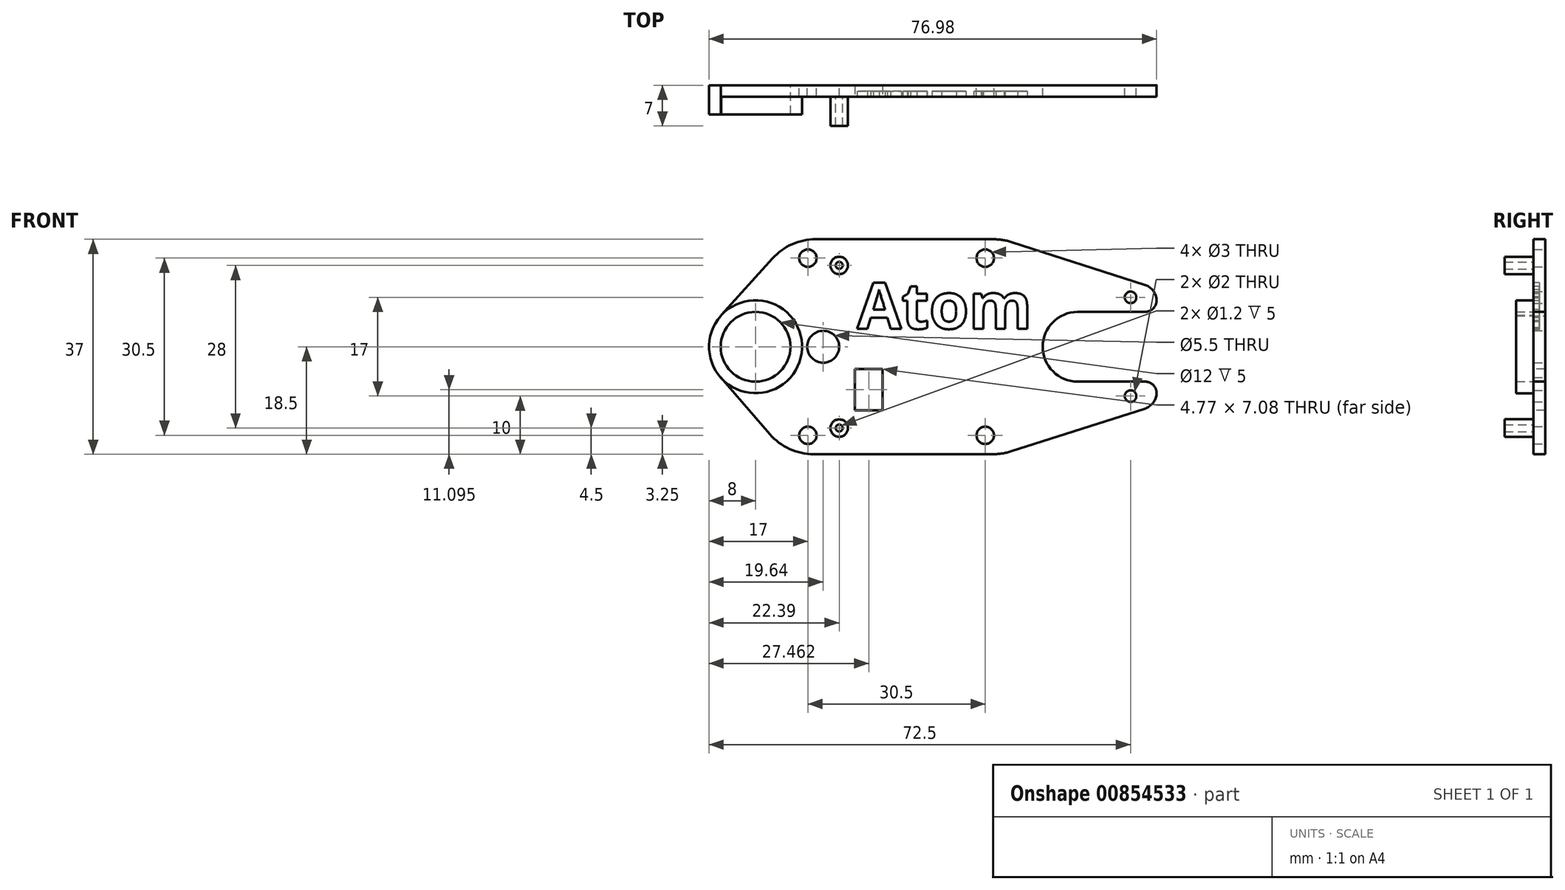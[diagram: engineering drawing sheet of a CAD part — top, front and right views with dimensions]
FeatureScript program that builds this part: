
annotation { "Feature Type Name" : "Feature", "Feature Type Description" : "" }
export const myFeature = defineFeature(function(context is Context, id is Id, definition is map)
    precondition{}
    {
        {
            var Q0;
            Q0=qCreatedBy(makeId("Front.planeOp"),FACE);
            var sketch = newSketch(context, id + "F0", { "sketchPlane" : qUnion([Q0])});
            skLineSegment(sketch, "E0.bottom", {"start": v(10.96, -18.5) * mm, "end": v(-26.06, -18.5) * mm});
            skLineSegment(sketch, "E0.top", {"start": v(11, 18.5) * mm, "end": v(-25.6, 18.5) * mm});
            skLineSegment(sketch, "E0.left", {"start": v(37.5, -10) * mm, "end": v(37.5, -6) * mm});
            skLineSegment(sketch, "E0.right", {"start": v(-37.5, -5.3) * mm, "end": v(-37.5, 5.3) * mm});
            skPoint(sketch, "E0.middle", {"position": v(0, 0) * mm});
            skPoint(sketch, "E1", {"position": v(-22.5, 15.25) * mm});
            skPoint(sketch, "E2", {"position": v(-22.5, -15.25) * mm});
            skPoint(sketch, "E3", {"position": v(8, 15.25) * mm});
            skPoint(sketch, "E4", {"position": v(8, -15.25) * mm});
            skPoint(sketch, "E5", {"position": v(33, 8.5) * mm});
            skPoint(sketch, "E6", {"position": v(33, -8.5) * mm});
            skCircle(sketch, "E7", {"center": v(-31.5, 0) * mm, "radius": 6 * mm});
            skCircle(sketch, "E8", {"center": v(-22.5, 15.25) * mm, "radius": 1.5 * mm});
            skCircle(sketch, "E9", {"center": v(-22.5, -15.25) * mm, "radius": 1.5 * mm});
            skCircle(sketch, "E10", {"center": v(8, 15.25) * mm, "radius": 1.5 * mm});
            skCircle(sketch, "E11", {"center": v(8, -15.25) * mm, "radius": 1.5 * mm});
            skCircle(sketch, "E12", {"center": v(33, 8.5) * mm, "radius": 1 * mm});
            skCircle(sketch, "E13", {"center": v(33, -8.5) * mm, "radius": 1 * mm});
            skCircle(sketch, "E14", {"center": v(-19.86, 0) * mm, "radius": 2.75 * mm});
            skCircle(sketch, "E15", {"center": v(-31.5, 0) * mm, "radius": 8 * mm});
            skLineSegment(sketch, "E16", {"start": v(-25.6, 18.5) * mm, "end": v(-37.5, 5.3) * mm});
            skLineSegment(sketch, "E17", {"start": v(-26.06, -18.5) * mm, "end": v(-37.5, -5.3) * mm});
            skPoint(sketch, "E18.orphan", {"position": v(-37.5, 18.5) * mm});
            skPoint(sketch, "E19.orphan", {"position": v(-37.5, -18.5) * mm});
            skPoint(sketch, "E20", {"position": v(37.5, -10) * mm});
            skPoint(sketch, "E21", {"position": v(37.5, 10) * mm});
            skLineSegment(sketch, "E22", {"start": v(11, 18.5) * mm, "end": v(37.5, 10) * mm});
            skLineSegment(sketch, "E23", {"start": v(10.96, -18.5) * mm, "end": v(37.5, -10) * mm});
            skPoint(sketch, "E24.orphan", {"position": v(37.5, 18.5) * mm});
            skPoint(sketch, "E25.orphan", {"position": v(37.5, -18.5) * mm});
            skPoint(sketch, "E26", {"position": v(37.5, 6) * mm});
            skPoint(sketch, "E27", {"position": v(37.5, -6) * mm});
            skLineSegment(sketch, "E28", {"start": v(37.5, 6) * mm, "end": v(23.9, 6) * mm});
            skLineSegment(sketch, "E29", {"start": v(37.5, -6) * mm, "end": v(23.9, -6) * mm});
            skArc(sketch, "E30", {"start": v(23.9, 6) * mm, "mid": v(17.9, 0) * mm, "end": v(23.9, -6) * mm});
            skLineSegment(sketch, "E31.trimOffspring", {"start": v(37.5, 6) * mm, "end": v(37.5, 10) * mm});
            skSolve(sketch);
        }
        {
            var Q0;
            Q0=makeQuery(id+"F0.imprint","IMPRINT",FACE,{"disambiguationData":[TD([[makeQuery(id+"F0.imprint","IMPRINT",EDGE,{"derivedFrom":sQuery(id+"F0.wireOp",EDGE,"E0.bottom")}),-1.0]])]});
            extrude(context, id + "F1", {"entities" : qUnion([Q0]), "depth" : 2 * mm, "offsetDistance" : 25 * mm});
        }
        {
            var Q0;
            {var subQ6=sQuery(id+"F0.wireOp",EDGE,"E7");Q0=makeQuery(id+"F0.imprint","IMPRINT",FACE,{"disambiguationData":[TD([[makeQuery(id+"F0.imprint","IMPRINT",EDGE,{"derivedFrom":subQ6}),-1.0]])]});}
            var Q1;
            {var subQ0=sQuery(id+"F0.wireOp",EDGE,"E15");var subQ1=sQuery(id+"F0.wireOp",EDGE,"E0.right");var subQ2=makeQuery(id+"F0.imprint","INTERSECT",VERTEX,{"derivedFrom":[subQ1,subQ0]});Q1=makeQuery(id+"F0.imprint","IMPRINT",FACE,{"disambiguationData":[TD([[makeQuery(id+"F0.imprint","IMPRINT",EDGE,{"disambiguationData":[TD([[subQ2,-1.0]])],"derivedFrom":subQ1}),1.0]])]});}
            extrude(context, id + "F2", {"entities" : qUnion([Q0, Q1]), "operationType" : NewBodyOperationType.ADD, "depth" : 5 * mm, "offsetDistance" : 25 * mm});
        }
        {
            var Q0;
            Q0=makeQuery(id+"F1.opExtrude","SWEPT_EDGE",EDGE,{"disambiguationData":[OSD([sQuery(id+"F0.wireOp",EDGE,"E0.top"),sQuery(id+"F0.wireOp",EDGE,"E16")])]});
            fillet(context, id + "F3", {"entities" : qUnion([Q0]), "radius" : 10 * mm, "tangentPropagation" : true, "allowEdgeOverflow" : false});
        }
        {
            var Q0;
            Q0=makeQuery(id+"F1.opExtrude","SWEPT_EDGE",EDGE,{"disambiguationData":[OSD([sQuery(id+"F0.wireOp",EDGE,"E0.top"),sQuery(id+"F0.wireOp",EDGE,"E22")])]});
            fillet(context, id + "F4", {"entities" : qUnion([Q0]), "radius" : 10 * mm, "tangentPropagation" : true, "allowEdgeOverflow" : false});
        }
        {
            var Q0;
            Q0=makeQuery(id+"F1.opExtrude","SWEPT_EDGE",EDGE,{"disambiguationData":[OSD([sQuery(id+"F0.wireOp",EDGE,"E0.bottom"),sQuery(id+"F0.wireOp",EDGE,"E17")])]});
            fillet(context, id + "F5", {"entities" : qUnion([Q0]), "radius" : 10 * mm, "tangentPropagation" : true, "allowEdgeOverflow" : false});
        }
        {
            var Q0;
            Q0=makeQuery(id+"F1.opExtrude","SWEPT_EDGE",EDGE,{"disambiguationData":[OSD([sQuery(id+"F0.wireOp",EDGE,"E0.bottom"),sQuery(id+"F0.wireOp",EDGE,"E23")])]});
            fillet(context, id + "F6", {"entities" : qUnion([Q0]), "radius" : 10 * mm, "tangentPropagation" : true, "allowEdgeOverflow" : false});
        }
        {
            var Q0;
            Q0=makeQuery(id+"F1.opExtrude","SWEPT_EDGE",EDGE,{"disambiguationData":[OSD([sQuery(id+"F0.wireOp",EDGE,"E0.left"),sQuery(id+"F0.wireOp",EDGE,"E23")])]});
            fillet(context, id + "F7", {"entities" : qUnion([Q0]), "radius" : 3 * mm, "tangentPropagation" : true, "allowEdgeOverflow" : false});
        }
        {
            var Q0;
            Q0=makeQuery(id+"F1.opExtrude","SWEPT_EDGE",EDGE,{"disambiguationData":[OSD([sQuery(id+"F0.wireOp",EDGE,"E0.left"),sQuery(id+"F0.wireOp",EDGE,"E29")])]});
            fillet(context, id + "F8", {"entities" : qUnion([Q0]), "radius" : 2 * mm, "tangentPropagation" : true, "allowEdgeOverflow" : false});
        }
        {
            var Q0;
            Q0=makeQuery(id+"F1.opExtrude","SWEPT_EDGE",EDGE,{"disambiguationData":[OSD([sQuery(id+"F0.wireOp",EDGE,"E22"),sQuery(id+"F0.wireOp",EDGE,"E31.trimOffspring")])]});
            fillet(context, id + "F9", {"entities" : qUnion([Q0]), "radius" : 3 * mm, "tangentPropagation" : true, "allowEdgeOverflow" : false});
        }
        {
            var Q0;
            Q0=makeQuery(id+"F1.opExtrude","SWEPT_EDGE",EDGE,{"disambiguationData":[OSD([sQuery(id+"F0.wireOp",EDGE,"E28"),sQuery(id+"F0.wireOp",EDGE,"E31.trimOffspring")])]});
            fillet(context, id + "F10", {"entities" : qUnion([Q0]), "radius" : 2 * mm, "tangentPropagation" : true, "allowEdgeOverflow" : false});
        }
        {
            var Q0;
            {var subQ0=sQuery(id+"F0.wireOp",EDGE,"E11");var subQ1=sQuery(id+"F0.wireOp",EDGE,"E10");var subQ2=sQuery(id+"F0.wireOp",EDGE,"E9");var subQ3=sQuery(id+"F0.wireOp",EDGE,"E8");var subQ4=sQuery(id+"F0.wireOp",EDGE,"E0.top");var subQ5=sQuery(id+"F0.wireOp",EDGE,"E0.bottom");var subQ6=sQuery(id+"F0.wireOp",EDGE,"E17");var subQ7=sQuery(id+"F0.wireOp",EDGE,"E22");var subQ8=sQuery(id+"F0.wireOp",EDGE,"E30");var subQ9=sQuery(id+"F0.wireOp",EDGE,"E29");var subQ10=sQuery(id+"F0.wireOp",EDGE,"E16");var subQ11=sQuery(id+"F0.wireOp",EDGE,"E28");var subQ12=sQuery(id+"F0.wireOp",EDGE,"E23");var subQ13=sQuery(id+"F0.wireOp",EDGE,"E31.trimOffspring");var subQ14=sQuery(id+"F0.wireOp",EDGE,"E0.right");var subQ15=sQuery(id+"F0.wireOp",EDGE,"E13");var subQ16=sQuery(id+"F0.wireOp",EDGE,"E15");var subQ17=sQuery(id+"F0.wireOp",EDGE,"E14");var subQ18=sQuery(id+"F0.wireOp",EDGE,"E12");var subQ19=sQuery(id+"F0.wireOp",EDGE,"E0.left");Q0=makeQuery(id+"FZaNgLCDl8hIjAt_1.boolean.opBoolean","SPLIT",FACE,{"disambiguationData":[TD([makeQuery(id+"F1.opExtrude","SWEPT_FACE",FACE,{"disambiguationData":[OSD([subQ5])]})])],"derivedFrom":makeQuery(id+"F1.opExtrude","CAP_FACE",FACE,{"disambiguationData":[OSD([subQ5,subQ4,subQ19,subQ14,subQ3,subQ2,subQ1,subQ0,subQ18,subQ15,subQ17,subQ16,subQ10,subQ6,subQ7,subQ12,subQ11,subQ9,subQ8,subQ13])],"isStart":false})});}
            var sketch = newSketch(context, id + "F11", { "sketchPlane" : qUnion([Q0])});
            skCircle(sketch, "E32", {"center": v(-17.11, 14) * mm, "radius": 1.5 * mm});
            skCircle(sketch, "E33", {"center": v(-17.11, -14) * mm, "radius": 1.5 * mm});
            skCircle(sketch, "E34", {"center": v(-17.11, 14) * mm, "radius": 0.6 * mm});
            skCircle(sketch, "E35", {"center": v(-17.11, -14) * mm, "radius": 0.6 * mm});
            skPoint(sketch, "E36.start.orphan", {"position": v(-17.11, 0) * mm});
            skSolve(sketch);
        }
        {
            var Q0;
            Q0=qSketchRegion(id+"F11",true);
            extrude(context, id + "F12", {"entities" : qUnion([Q0]), "operationType" : NewBodyOperationType.ADD, "depth" : 5 * mm, "offsetDistance" : 25 * mm});
        }
        {
            var Q0;
            {var subQ0=sQuery(id+"F0.wireOp",EDGE,"E17");var subQ1=sQuery(id+"F0.wireOp",EDGE,"E0.bottom");var subQ2=sQuery(id+"F0.wireOp",EDGE,"E16");var subQ3=sQuery(id+"F0.wireOp",EDGE,"E0.top");var subQ4=sQuery(id+"F0.wireOp",EDGE,"E15");var subQ5=sQuery(id+"F0.wireOp",EDGE,"E22");var subQ6=sQuery(id+"F0.wireOp",EDGE,"E8");var subQ7=sQuery(id+"F0.wireOp",EDGE,"E30");var subQ8=sQuery(id+"F0.wireOp",EDGE,"E29");var subQ9=sQuery(id+"F0.wireOp",EDGE,"E28");var subQ10=sQuery(id+"F0.wireOp",EDGE,"E23");var subQ11=sQuery(id+"F0.wireOp",EDGE,"E31.trimOffspring");var subQ12=sQuery(id+"F0.wireOp",EDGE,"E0.right");var subQ13=sQuery(id+"F0.wireOp",EDGE,"E13");var subQ14=sQuery(id+"F0.wireOp",EDGE,"E9");var subQ15=sQuery(id+"F0.wireOp",EDGE,"E10");var subQ16=sQuery(id+"F0.wireOp",EDGE,"E11");var subQ17=sQuery(id+"F0.wireOp",EDGE,"E12");var subQ18=sQuery(id+"F0.wireOp",EDGE,"E14");var subQ19=sQuery(id+"F0.wireOp",EDGE,"E0.left");Q0=makeQuery(id+"F12.boolean.opBoolean","SPLIT",FACE,{"disambiguationData":[TD([makeQuery(id+"F1.opExtrude","SWEPT_FACE",FACE,{"disambiguationData":[OSD([subQ1])]})])],"derivedFrom":makeQuery(id+"F1.opExtrude","CAP_FACE",FACE,{"disambiguationData":[OSD([subQ1,subQ3,subQ19,subQ12,subQ6,subQ14,subQ15,subQ16,subQ17,subQ13,subQ18,subQ4,subQ2,subQ0,subQ5,subQ10,subQ9,subQ8,subQ7,subQ11])],"isStart":false})});}
            var sketch = newSketch(context, id + "F13", { "sketchPlane" : qUnion([Q0])});
            skLineSegment(sketch, "E37.bottom", {"start": v(-14.42, -3.86) * mm, "end": v(-9.65, -3.86) * mm});
            skLineSegment(sketch, "E37.top", {"start": v(-14.42, -10.95) * mm, "end": v(-9.65, -10.95) * mm});
            skLineSegment(sketch, "E37.left", {"start": v(-14.42, -3.86) * mm, "end": v(-14.42, -10.95) * mm});
            skLineSegment(sketch, "E37.right", {"start": v(-9.65, -3.86) * mm, "end": v(-9.65, -10.95) * mm});
            skSolve(sketch);
        }
        {
            var Q0;
            Q0=makeQuery(id+"F13.imprint","IMPRINT",FACE,{"disambiguationData":[TD([[makeQuery(id+"F13.imprint","IMPRINT",EDGE,{"derivedFrom":sQuery(id+"F13.wireOp",EDGE,"E37.bottom")}),-1.0]])]});
            extrude(context, id + "F14", {"entities" : qUnion([Q0]), "operationType" : NewBodyOperationType.REMOVE, "oppositeDirection" : true, "depth" : 2 * mm, "offsetDistance" : 25 * mm});
        }
        {
            var Q0;
            {var subQ0=sQuery(id+"F0.wireOp",EDGE,"E17");var subQ1=sQuery(id+"F0.wireOp",EDGE,"E0.bottom");var subQ2=sQuery(id+"F0.wireOp",EDGE,"E16");var subQ3=sQuery(id+"F0.wireOp",EDGE,"E0.top");var subQ4=sQuery(id+"F0.wireOp",EDGE,"E15");var subQ5=sQuery(id+"F0.wireOp",EDGE,"E22");var subQ6=sQuery(id+"F0.wireOp",EDGE,"E8");var subQ7=sQuery(id+"F0.wireOp",EDGE,"E30");var subQ8=sQuery(id+"F0.wireOp",EDGE,"E29");var subQ9=sQuery(id+"F0.wireOp",EDGE,"E28");var subQ10=sQuery(id+"F0.wireOp",EDGE,"E23");var subQ11=sQuery(id+"F0.wireOp",EDGE,"E31.trimOffspring");var subQ12=sQuery(id+"F0.wireOp",EDGE,"E0.right");var subQ13=sQuery(id+"F0.wireOp",EDGE,"E13");var subQ14=sQuery(id+"F0.wireOp",EDGE,"E9");var subQ15=sQuery(id+"F0.wireOp",EDGE,"E10");var subQ16=sQuery(id+"F0.wireOp",EDGE,"E11");var subQ17=sQuery(id+"F0.wireOp",EDGE,"E12");var subQ18=sQuery(id+"F0.wireOp",EDGE,"E14");var subQ19=sQuery(id+"F0.wireOp",EDGE,"E0.left");Q0=makeQuery(id+"F12.boolean.opBoolean","SPLIT",FACE,{"disambiguationData":[TD([makeQuery(id+"F1.opExtrude","SWEPT_FACE",FACE,{"disambiguationData":[OSD([subQ1])]})])],"derivedFrom":makeQuery(id+"F1.opExtrude","CAP_FACE",FACE,{"disambiguationData":[OSD([subQ1,subQ3,subQ19,subQ12,subQ6,subQ14,subQ15,subQ16,subQ17,subQ13,subQ18,subQ4,subQ2,subQ0,subQ5,subQ10,subQ9,subQ8,subQ7,subQ11])],"isStart":false})});}
            var sketch = newSketch(context, id + "F15", { "sketchPlane" : qUnion([Q0])});
            skText(sketch, "E38", { "text": "Atom", "fontName": "OpenSans-Bold.ttf"});
            const initialGuessF15  = {"E38": [-0.01406, 0.0031, 1, 0, 0.00795]};
            skSetInitialGuess(sketch, initialGuessF15);
            skSolve(sketch);
        }
        {
            var Q0;
            Q0=qSketchRegion(id+"F15",true);
            extrude(context, id + "F16", {"entities" : qUnion([Q0]), "operationType" : NewBodyOperationType.REMOVE, "oppositeDirection" : true, "depth" : 1 * mm, "offsetDistance" : 25 * mm});
        }
    });
